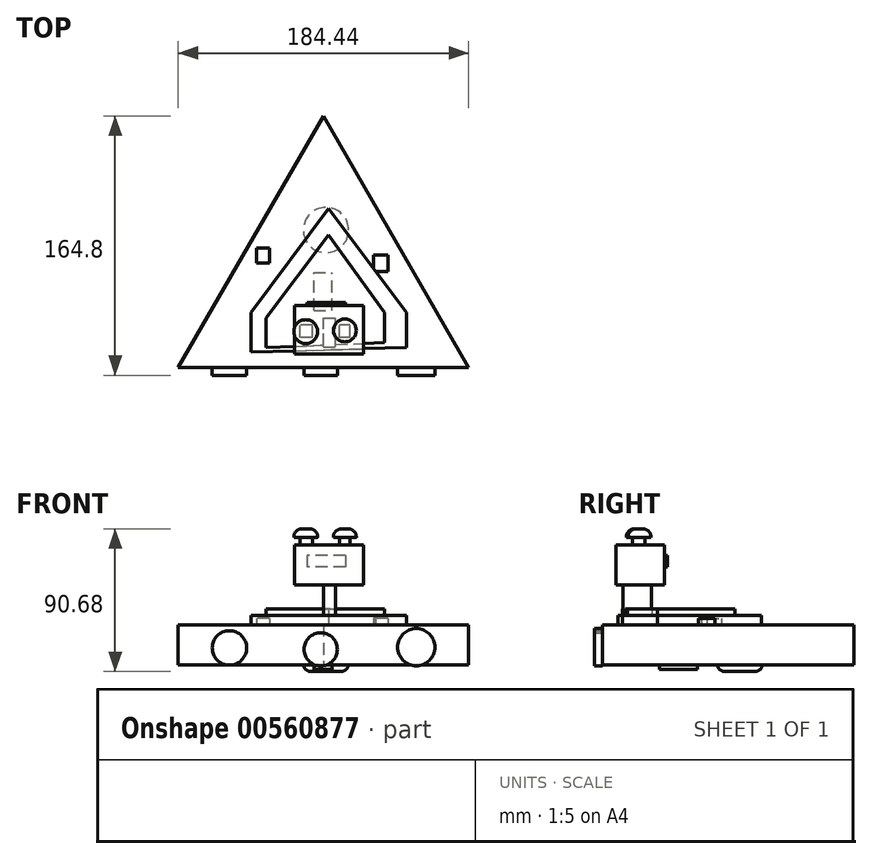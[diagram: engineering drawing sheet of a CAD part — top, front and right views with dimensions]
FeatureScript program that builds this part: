
annotation { "Feature Type Name" : "Feature", "Feature Type Description" : "" }
export const myFeature = defineFeature(function(context is Context, id is Id, definition is map)
    precondition{}
    {
        {
            var Q0;
            Q0=qCreatedBy(makeId("Top.planeOp"),FACE);
            var sketch = newSketch(context, id + "F0", { "sketchPlane" : qUnion([Q0])});
            skCircle(sketch, "E0.cCircle", {"center": v(0, 0) * mm, "radius": 53.24 * mm, "construction": true});
            skLineSegment(sketch, "E0.0", {"start": v(92.22, -53.24) * mm, "end": v(-92.22, -53.24) * mm});
            skLineSegment(sketch, "E0.1", {"start": v(-92.22, -53.24) * mm, "end": v(0, 106.48) * mm});
            skLineSegment(sketch, "E0.2", {"start": v(0, 106.48) * mm, "end": v(92.22, -53.24) * mm});
            skPoint(sketch, "E0.0.midPoint", {"position": v(0, -53.24) * mm});
            skSolve(sketch);
        }
        {
            var Q0;
            Q0=makeQuery(id+"F0.imprint","IMPRINT",FACE,{"disambiguationData":[TD([[makeQuery(id+"F0.imprint","IMPRINT",EDGE,{"derivedFrom":sQuery(id+"F0.wireOp",EDGE,"E0.0")}),-1.0]])]});
            extrude(context, id + "F1", {"entities" : qUnion([Q0]), "depth" : 25.4 * mm, "offsetDistance" : 25.4 * mm});
        }
        {
            var Q0;
            Q0=makeQuery(id+"F1.opExtrude","CAP_FACE",FACE,{"disambiguationData":[OSD([sQuery(id+"F0.wireOp",EDGE,"E0.0"),sQuery(id+"F0.wireOp",EDGE,"E0.1"),sQuery(id+"F0.wireOp",EDGE,"E0.2")])],"isStart":false});
            var sketch = newSketch(context, id + "F2", { "sketchPlane" : qUnion([Q0])});
            skLineSegment(sketch, "E1.bottom", {"start": v(0, -40.26) * mm, "end": v(7.7, -40.26) * mm});
            skLineSegment(sketch, "E1.top", {"start": v(0, -22.03) * mm, "end": v(7.7, -22.03) * mm});
            skLineSegment(sketch, "E1.left", {"start": v(0, -40.26) * mm, "end": v(0, -22.03) * mm});
            skLineSegment(sketch, "E1.right", {"start": v(7.7, -40.26) * mm, "end": v(7.7, -22.03) * mm});
            skSolve(sketch);
        }
        {
            var Q0;
            Q0=makeQuery(id+"F2.imprint","IMPRINT",FACE,{"disambiguationData":[TD([[makeQuery(id+"F2.imprint","IMPRINT",EDGE,{"derivedFrom":sQuery(id+"F2.wireOp",EDGE,"E1.bottom")}),1.0]])]});
            extrude(context, id + "F3", {"entities" : qUnion([Q0]), "operationType" : NewBodyOperationType.ADD, "depth" : 25.4 * mm, "offsetDistance" : 25.4 * mm});
        }
        {
            var Q0;
            Q0=makeQuery(id+"F3.opExtrude","CAP_FACE",FACE,{"disambiguationData":[OSD([sQuery(id+"F2.wireOp",EDGE,"E1.bottom"),sQuery(id+"F2.wireOp",EDGE,"E1.top"),sQuery(id+"F2.wireOp",EDGE,"E1.left"),sQuery(id+"F2.wireOp",EDGE,"E1.right")])],"isStart":false});
            var sketch = newSketch(context, id + "F4", { "sketchPlane" : qUnion([Q0])});
            skLineSegment(sketch, "E2.bottom", {"start": v(25.6, -44.69) * mm, "end": v(-18.21, -44.69) * mm});
            skLineSegment(sketch, "E2.top", {"start": v(25.6, -13.9) * mm, "end": v(-18.21, -13.9) * mm});
            skLineSegment(sketch, "E2.left", {"start": v(25.6, -44.69) * mm, "end": v(25.6, -13.9) * mm});
            skLineSegment(sketch, "E2.right", {"start": v(-18.21, -44.69) * mm, "end": v(-18.21, -13.9) * mm});
            skSolve(sketch);
        }
        {
            var Q0;
            Q0 = qSketchRegion(id + "F4", true);
            extrude(context, id + "F5", {"entities" : qUnion([Q0]), "operationType" : NewBodyOperationType.ADD, "depth" : 25.4 * mm, "offsetDistance" : 25.4 * mm});
        }
        {
            var Q0;
            Q0=makeQuery(id+"F1.opExtrude","CAP_FACE",FACE,{"disambiguationData":[OSD([sQuery(id+"F0.wireOp",EDGE,"E0.0"),sQuery(id+"F0.wireOp",EDGE,"E0.1"),sQuery(id+"F0.wireOp",EDGE,"E0.2")])],"isStart":false});
            var sketch = newSketch(context, id + "F6", { "sketchPlane" : qUnion([Q0])});
            skLineSegment(sketch, "E3", {"start": v(52.67, -40.6) * mm, "end": v(52.67, -18.36) * mm});
            skLineSegment(sketch, "E4", {"start": v(52.67, -18.36) * mm, "end": v(3.39, 47.75) * mm});
            skLineSegment(sketch, "E5", {"start": v(3.39, 47.75) * mm, "end": v(-45.97, -18.36) * mm});
            skLineSegment(sketch, "E6", {"start": v(-45.97, -18.36) * mm, "end": v(-45.97, -43.57) * mm});
            skLineSegment(sketch, "E7", {"start": v(-45.97, -43.57) * mm, "end": v(52.67, -40.6) * mm});
            skSolve(sketch);
        }
        {
            var Q0;
            Q0 = qSketchRegion(id + "F6", true);
            extrude(context, id + "F7", {"entities" : qUnion([Q0]), "operationType" : NewBodyOperationType.ADD, "depth" : 5.84 * mm, "offsetDistance" : 25.4 * mm});
        }
        {
            var Q0;
            Q0=makeQuery(id+"F7.opExtrude","CAP_FACE",FACE,{"disambiguationData":[OSD([sQuery(id+"F6.wireOp",EDGE,"E3"),sQuery(id+"F6.wireOp",EDGE,"E4"),sQuery(id+"F6.wireOp",EDGE,"E5"),sQuery(id+"F6.wireOp",EDGE,"E6"),sQuery(id+"F6.wireOp",EDGE,"E7")])],"isStart":false});
            var sketch = newSketch(context, id + "F8", { "sketchPlane" : qUnion([Q0])});
            skLineSegment(sketch, "E8", {"start": v(38.9, -37.54) * mm, "end": v(38.9, -18.36) * mm});
            skLineSegment(sketch, "E9", {"start": v(38.9, -18.36) * mm, "end": v(3.39, 30.95) * mm});
            skLineSegment(sketch, "E10", {"start": v(3.39, 30.95) * mm, "end": v(-36.38, -21.88) * mm});
            skLineSegment(sketch, "E11", {"start": v(-36.38, -21.88) * mm, "end": v(-36.38, -40.6) * mm});
            skLineSegment(sketch, "E12", {"start": v(-36.38, -40.6) * mm, "end": v(38.9, -37.54) * mm});
            skSolve(sketch);
        }
        {
            var Q0;
            Q0 = qSketchRegion(id + "F8", true);
            extrude(context, id + "F9", {"entities" : qUnion([Q0]), "operationType" : NewBodyOperationType.ADD, "depth" : 4.32 * mm, "offsetDistance" : 25.4 * mm});
        }
        {
            var Q0;
            Q0=makeQuery(id+"F1.opExtrude","SWEPT_FACE",FACE,{"disambiguationData":[OSD([sQuery(id+"F0.wireOp",EDGE,"E0.0")])]});
            var sketch = newSketch(context, id + "F10", { "sketchPlane" : qUnion([Q0])});
            skCircle(sketch, "E13", {"center": v(-59.66, 10.74) * mm, "radius": 10.94 * mm});
            skCircle(sketch, "E14", {"center": v(-1.67, 9.8) * mm, "radius": 10.56 * mm});
            skCircle(sketch, "E15", {"center": v(59.02, 11.17) * mm, "radius": 11.85 * mm});
            skSolve(sketch);
        }
        {
            var Q0;
            Q0 = qSketchRegion(id + "F10", true);
            extrude(context, id + "F11", {"entities" : qUnion([Q0]), "depth" : 5.08 * mm, "offsetDistance" : 25.4 * mm});
        }
        {
            var Q0;
            Q0=makeQuery(id+"F1.opExtrude","CAP_FACE",FACE,{"disambiguationData":[OSD([sQuery(id+"F0.wireOp",EDGE,"E0.0"),sQuery(id+"F0.wireOp",EDGE,"E0.1"),sQuery(id+"F0.wireOp",EDGE,"E0.2")])],"isStart":true});
            var sketch = newSketch(context, id + "F12", { "sketchPlane" : qUnion([Q0])});
            skLineSegment(sketch, "E16.bottom", {"start": v(-6.04, 17.09) * mm, "end": v(5.52, 17.09) * mm});
            skLineSegment(sketch, "E16.top", {"start": v(-6.04, -6.95) * mm, "end": v(5.52, -6.95) * mm});
            skLineSegment(sketch, "E16.left", {"start": v(-6.04, 17.09) * mm, "end": v(-6.04, -6.95) * mm});
            skLineSegment(sketch, "E16.right", {"start": v(5.52, 17.09) * mm, "end": v(5.52, -6.95) * mm});
            skSolve(sketch);
        }
        {
            var Q0;
            Q0 = qSketchRegion(id + "F12", true);
            extrude(context, id + "F13", {"entities" : qUnion([Q0]), "depth" : 3.05 * mm, "offsetDistance" : 25.4 * mm});
        }
        {
            var Q0;
            Q0=makeQuery(id+"F1.opExtrude","CAP_FACE",FACE,{"disambiguationData":[OSD([sQuery(id+"F0.wireOp",EDGE,"E0.0"),sQuery(id+"F0.wireOp",EDGE,"E0.1"),sQuery(id+"F0.wireOp",EDGE,"E0.2")])],"isStart":true});
            var sketch = newSketch(context, id + "F14", { "sketchPlane" : qUnion([Q0])});
            skCircle(sketch, "E17", {"center": v(1.62, -33.97) * mm, "radius": 14.39 * mm});
            skSolve(sketch);
        }
        {
            var Q0;
            Q0 = qSketchRegion(id + "F14", true);
            extrude(context, id + "F15", {"entities" : qUnion([Q0]), "operationType" : NewBodyOperationType.ADD, "depth" : 4.32 * mm, "offsetDistance" : 25.4 * mm});
        }
        {
            var Q0;
            Q0=makeQuery(id+"F15.opExtrude","CAP_EDGE",EDGE,{"disambiguationData":[OSD([sQuery(id+"F14.wireOp",EDGE,"E17")])],"isStart":false});
            fillet(context, id + "F16", {"entities" : qUnion([Q0]), "radius" : 5.08 * mm, "tangentPropagation" : true, "allowEdgeOverflow" : false});
        }
        {
            var Q0;
            Q0=makeQuery(id+"F5.opExtrude","SWEPT_FACE",FACE,{"disambiguationData":[OSD([sQuery(id+"F4.wireOp",EDGE,"E2.top")])]});
            var sketch = newSketch(context, id + "F17", { "sketchPlane" : qUnion([Q0])});
            skLineSegment(sketch, "E18.bottom", {"start": v(-14.06, 69.44) * mm, "end": v(10.47, 69.44) * mm});
            skLineSegment(sketch, "E18.top", {"start": v(-14.06, 62.28) * mm, "end": v(10.47, 62.28) * mm});
            skLineSegment(sketch, "E18.left", {"start": v(-14.06, 69.44) * mm, "end": v(-14.06, 62.28) * mm});
            skLineSegment(sketch, "E18.right", {"start": v(10.47, 69.44) * mm, "end": v(10.47, 62.28) * mm});
            skSolve(sketch);
        }
        {
            var Q0;
            Q0 = qSketchRegion(id + "F17", true);
            extrude(context, id + "F18", {"entities" : qUnion([Q0]), "depth" : 1.78 * mm, "offsetDistance" : 25.4 * mm});
        }
        {
            var Q0;
            Q0=makeQuery(id+"F1.opExtrude","CAP_FACE",FACE,{"disambiguationData":[OSD([sQuery(id+"F0.wireOp",EDGE,"E0.0"),sQuery(id+"F0.wireOp",EDGE,"E0.1"),sQuery(id+"F0.wireOp",EDGE,"E0.2")])],"isStart":false});
            var sketch = newSketch(context, id + "F19", { "sketchPlane" : qUnion([Q0])});
            skLineSegment(sketch, "E19.bottom", {"start": v(-34.25, 13.14) * mm, "end": v(-42.34, 13.14) * mm});
            skLineSegment(sketch, "E19.top", {"start": v(-34.25, 22.42) * mm, "end": v(-42.34, 22.42) * mm});
            skLineSegment(sketch, "E19.left", {"start": v(-34.25, 13.14) * mm, "end": v(-34.25, 22.42) * mm});
            skLineSegment(sketch, "E19.right", {"start": v(-42.34, 13.14) * mm, "end": v(-42.34, 22.42) * mm});
            skLineSegment(sketch, "E20.bottom", {"start": v(41.17, 7.57) * mm, "end": v(31.73, 7.57) * mm});
            skLineSegment(sketch, "E20.top", {"start": v(41.17, 18.2) * mm, "end": v(31.73, 18.2) * mm});
            skLineSegment(sketch, "E20.left", {"start": v(41.17, 7.57) * mm, "end": v(41.17, 18.2) * mm});
            skLineSegment(sketch, "E20.right", {"start": v(31.73, 7.57) * mm, "end": v(31.73, 18.2) * mm});
            skSolve(sketch);
        }
        {
            var Q0;
            Q0 = qSketchRegion(id + "F19", true);
            extrude(context, id + "F20", {"entities" : qUnion([Q0]), "operationType" : NewBodyOperationType.ADD, "depth" : 4.06 * mm, "offsetDistance" : 25.4 * mm});
        }
        {
            var Q0;
            Q0=makeQuery(id+"F5.opExtrude","CAP_FACE",FACE,{"disambiguationData":[OSD([sQuery(id+"F4.wireOp",EDGE,"E2.bottom"),sQuery(id+"F4.wireOp",EDGE,"E2.top"),sQuery(id+"F4.wireOp",EDGE,"E2.left"),sQuery(id+"F4.wireOp",EDGE,"E2.right")])],"isStart":false});
            var sketch = newSketch(context, id + "F21", { "sketchPlane" : qUnion([Q0])});
            skLineSegment(sketch, "E21.bottom", {"start": v(17, -34.28) * mm, "end": v(10.3, -34.28) * mm});
            skLineSegment(sketch, "E21.top", {"start": v(17, -26.24) * mm, "end": v(10.3, -26.24) * mm});
            skLineSegment(sketch, "E21.left", {"start": v(17, -34.28) * mm, "end": v(17, -26.24) * mm});
            skLineSegment(sketch, "E21.right", {"start": v(10.3, -34.28) * mm, "end": v(10.3, -26.24) * mm});
            skPoint(sketch, "E22.firstSnap0", {"position": v(13.65, -34.28) * mm});
            skLineSegment(sketch, "E22.bottom", {"start": v(-7.03, -34.28) * mm, "end": v(-14.99, -34.28) * mm});
            skLineSegment(sketch, "E22.top", {"start": v(-7.03, -26.19) * mm, "end": v(-14.99, -26.19) * mm});
            skLineSegment(sketch, "E22.left", {"start": v(-7.03, -34.28) * mm, "end": v(-7.03, -26.19) * mm});
            skLineSegment(sketch, "E22.right", {"start": v(-14.99, -34.28) * mm, "end": v(-14.99, -26.19) * mm});
            skSolve(sketch);
        }
        {
            var Q0;
            Q0 = qSketchRegion(id + "F21", true);
            extrude(context, id + "F22", {"entities" : qUnion([Q0]), "depth" : 4.83 * mm, "offsetDistance" : 25.4 * mm});
        }
        {
            var Q0;
            Q0=makeQuery(id+"F22.opExtrude","CAP_FACE",FACE,{"disambiguationData":[OSD([sQuery(id+"F21.wireOp",EDGE,"E21.bottom"),sQuery(id+"F21.wireOp",EDGE,"E21.top"),sQuery(id+"F21.wireOp",EDGE,"E21.left"),sQuery(id+"F21.wireOp",EDGE,"E21.right")])],"isStart":false});
            var sketch = newSketch(context, id + "F23", { "sketchPlane" : qUnion([Q0])});
            skCircle(sketch, "E23", {"center": v(13.65, -29.77) * mm, "radius": 7.25 * mm});
            skCircle(sketch, "E24", {"center": v(-11.19, -30.56) * mm, "radius": 7.57 * mm});
            skSolve(sketch);
        }
        {
            var Q0;
            Q0 = qSketchRegion(id + "F23", true);
            extrude(context, id + "F24", {"entities" : qUnion([Q0]), "depth" : 5.33 * mm, "offsetDistance" : 25.4 * mm});
        }
        {
            var Q0;
            Q0=makeQuery(id+"F24.opExtrude","CAP_EDGE",EDGE,{"disambiguationData":[OSD([sQuery(id+"F23.wireOp",EDGE,"E24")])],"isStart":false});
            fillet(context, id + "F25", {"entities" : qUnion([Q0]), "radius" : 5.08 * mm, "tangentPropagation" : true, "allowEdgeOverflow" : false});
        }
        {
            var Q0;
            Q0=makeQuery(id+"F24.opExtrude","CAP_FACE",FACE,{"disambiguationData":[OSD([sQuery(id+"F23.wireOp",EDGE,"E23")])],"isStart":false});
            fillet(context, id + "F26", {"entities" : qUnion([Q0]), "radius" : 5.08 * mm, "tangentPropagation" : true, "allowEdgeOverflow" : false});
        }
    });
